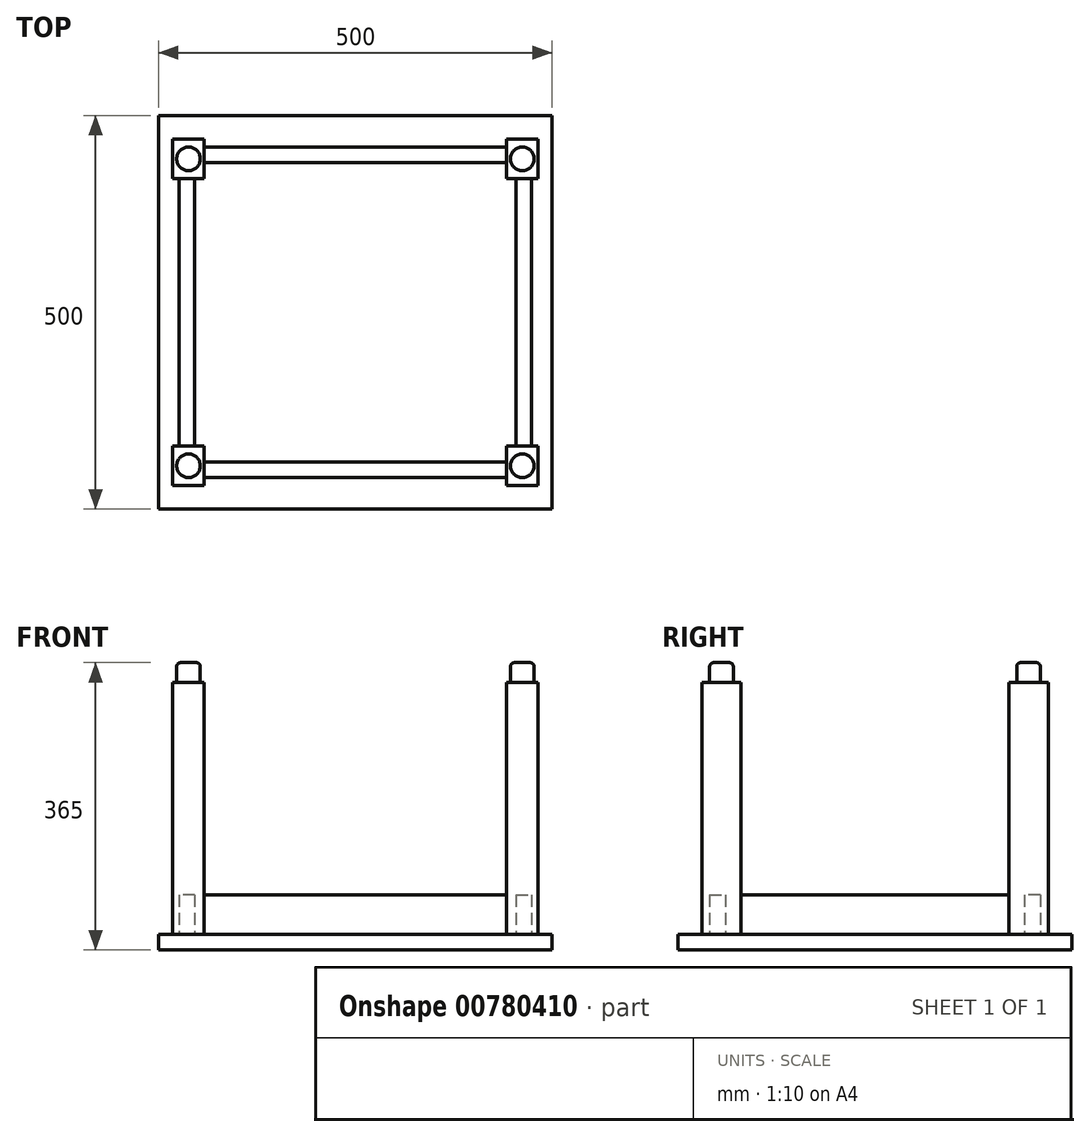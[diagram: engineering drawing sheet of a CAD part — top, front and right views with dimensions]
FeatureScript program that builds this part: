
annotation { "Feature Type Name" : "Feature", "Feature Type Description" : "" }
export const myFeature = defineFeature(function(context is Context, id is Id, definition is map)
    precondition{}
    {
        {
            var Q0;
            Q0=qCreatedBy(makeId("Top.planeOp"),FACE);
            var sketch = newSketch(context, id + "F0", { "sketchPlane" : qUnion([Q0])});
            skLineSegment(sketch, "E0.bottom", {"start": v(250, 250) * mm, "end": v(-250, 250) * mm});
            skLineSegment(sketch, "E0.top", {"start": v(250, -250) * mm, "end": v(-250, -250) * mm});
            skLineSegment(sketch, "E0.left", {"start": v(250, 250) * mm, "end": v(250, -250) * mm});
            skLineSegment(sketch, "E0.right", {"start": v(-250, 250) * mm, "end": v(-250, -250) * mm});
            skPoint(sketch, "E0.middle", {"position": v(0, 0) * mm});
            skSolve(sketch);
        }
        {
            var Q0;
            Q0 = qSketchRegion(id + "F0", true);
            extrude(context, id + "F1", {"entities" : qUnion([Q0]), "depth" : 20 * mm, "offsetDistance" : 25 * mm});
        }
        {
            var Q0;
            Q0=makeQuery(id+"F1.opExtrude","CAP_FACE",FACE,{"disambiguationData":[OSD([sQuery(id+"F0.wireOp",EDGE,"E0.bottom"),sQuery(id+"F0.wireOp",EDGE,"E0.top"),sQuery(id+"F0.wireOp",EDGE,"E0.left"),sQuery(id+"F0.wireOp",EDGE,"E0.right")])],"isStart":false});
            var sketch = newSketch(context, id + "F2", { "sketchPlane" : qUnion([Q0])});
            skLineSegment(sketch, "E1.bottom", {"start": v(212, 195) * mm, "end": v(-212, 195) * mm, "construction": true});
            skLineSegment(sketch, "E1.top", {"start": v(212, -195) * mm, "end": v(-212, -195) * mm, "construction": true});
            skLineSegment(sketch, "E1.left", {"start": v(212, 195) * mm, "end": v(212, -195) * mm, "construction": true});
            skLineSegment(sketch, "E1.right", {"start": v(-212, 195) * mm, "end": v(-212, -195) * mm, "construction": true});
            skPoint(sketch, "E1.middle", {"position": v(0, 0) * mm});
            skLineSegment(sketch, "E2.bottom", {"start": v(-192, 220) * mm, "end": v(-232, 220) * mm});
            skLineSegment(sketch, "E2.top", {"start": v(-192, 170) * mm, "end": v(-232, 170) * mm});
            skLineSegment(sketch, "E2.left", {"start": v(-192, 220) * mm, "end": v(-192, 170) * mm});
            skLineSegment(sketch, "E2.right", {"start": v(-232, 220) * mm, "end": v(-232, 170) * mm});
            skPoint(sketch, "E2.middle", {"position": v(-212, 195) * mm});
            skLineSegment(sketch, "E3", {"start": v(-212, 0) * mm, "end": v(212, 0) * mm, "construction": true});
            skLineSegment(sketch, "E4", {"start": v(0, 195) * mm, "end": v(0, -195) * mm, "construction": true});
            skLineSegment(sketch, "E5.MirrorCS", {"start": v(192, 220) * mm, "end": v(232, 220) * mm});
            skLineSegment(sketch, "E6.MirrorCS", {"start": v(192, 170) * mm, "end": v(232, 170) * mm});
            skLineSegment(sketch, "E7.MirrorCS", {"start": v(232, 220) * mm, "end": v(232, 170) * mm});
            skLineSegment(sketch, "E8.MirrorCS", {"start": v(192, 220) * mm, "end": v(192, 170) * mm});
            skPoint(sketch, "E9.MirrorP", {"position": v(212, 195) * mm});
            skLineSegment(sketch, "E10.MirrorCS", {"start": v(-212, 195) * mm, "end": v(212, 195) * mm, "construction": true});
            skLineSegment(sketch, "E11.MirrorCS", {"start": v(-192, -220) * mm, "end": v(-192, -170) * mm});
            skLineSegment(sketch, "E12.MirrorCS", {"start": v(192, -220) * mm, "end": v(192, -170) * mm});
            skPoint(sketch, "E13.MirrorP", {"position": v(-212, -195) * mm});
            skPoint(sketch, "E14.MirrorP", {"position": v(212, -195) * mm});
            skLineSegment(sketch, "E15.MirrorCS", {"start": v(232, -220) * mm, "end": v(232, -170) * mm});
            skLineSegment(sketch, "E16.MirrorCS", {"start": v(-232, -220) * mm, "end": v(-232, -170) * mm});
            skLineSegment(sketch, "E17.MirrorCS", {"start": v(-212, -195) * mm, "end": v(212, -195) * mm, "construction": true});
            skLineSegment(sketch, "E18.MirrorCS", {"start": v(192, -170) * mm, "end": v(232, -170) * mm});
            skLineSegment(sketch, "E19.MirrorCS", {"start": v(-192, -220) * mm, "end": v(-232, -220) * mm});
            skLineSegment(sketch, "E20.MirrorCS", {"start": v(-192, -170) * mm, "end": v(-232, -170) * mm});
            skLineSegment(sketch, "E21.MirrorCS", {"start": v(192, -220) * mm, "end": v(232, -220) * mm});
            skSolve(sketch);
        }
        {
            var Q0;
            Q0=makeQuery(id+"F2.imprint","IMPRINT",FACE,{"disambiguationData":[TD([[makeQuery(id+"F2.imprint","IMPRINT",EDGE,{"derivedFrom":sQuery(id+"F2.wireOp",EDGE,"E7.MirrorCS")}),-1.0]])]});
            var Q1;
            Q1=makeQuery(id+"F2.imprint","IMPRINT",FACE,{"disambiguationData":[TD([[makeQuery(id+"F2.imprint","IMPRINT",EDGE,{"derivedFrom":sQuery(id+"F2.wireOp",EDGE,"E11.MirrorCS")}),1.0]])]});
            var Q2;
            Q2=makeQuery(id+"F2.imprint","IMPRINT",FACE,{"disambiguationData":[TD([[makeQuery(id+"F2.imprint","IMPRINT",EDGE,{"derivedFrom":sQuery(id+"F2.wireOp",EDGE,"E15.MirrorCS")}),1.0]])]});
            var Q3;
            Q3=makeQuery(id+"F2.imprint","IMPRINT",FACE,{"disambiguationData":[TD([[makeQuery(id+"F2.imprint","IMPRINT",EDGE,{"derivedFrom":sQuery(id+"F2.wireOp",EDGE,"E2.left")}),-1.0]])]});
            extrude(context, id + "F3", {"entities" : qUnion([Q0, Q1, Q2, Q3]), "operationType" : NewBodyOperationType.ADD, "depth" : 320 * mm, "offsetDistance" : 25 * mm});
        }
        {
            var Q0;
            Q0=makeQuery(id+"F1.opExtrude","CAP_FACE",FACE,{"disambiguationData":[OSD([sQuery(id+"F0.wireOp",EDGE,"E0.bottom"),sQuery(id+"F0.wireOp",EDGE,"E0.top"),sQuery(id+"F0.wireOp",EDGE,"E0.left"),sQuery(id+"F0.wireOp",EDGE,"E0.right")])],"isStart":false});
            var sketch = newSketch(context, id + "F4", { "sketchPlane" : qUnion([Q0])});
            skLineSegment(sketch, "E22", {"start": v(-192, -210) * mm, "end": v(192, -210) * mm});
            skLineSegment(sketch, "E23", {"start": v(0, 0) * mm, "end": v(-294.35, 0) * mm, "construction": true});
            skLineSegment(sketch, "E24.MirrorCS", {"start": v(-192, 210) * mm, "end": v(-192, 199.43) * mm});
            skLineSegment(sketch, "E25.MirrorCS", {"start": v(192, 195) * mm, "end": v(192, 210) * mm});
            skLineSegment(sketch, "E26.MirrorCS", {"start": v(-192, 210) * mm, "end": v(192, 210) * mm});
            skLineSegment(sketch, "E27", {"start": v(-192, -190) * mm, "end": v(192, -190) * mm});
            skLineSegment(sketch, "E28", {"start": v(-192, -210) * mm, "end": v(-192, -190) * mm});
            skLineSegment(sketch, "E29", {"start": v(192, -210) * mm, "end": v(192, -190) * mm});
            skLineSegment(sketch, "E30", {"start": v(192, 210) * mm, "end": v(192, 190) * mm});
            skLineSegment(sketch, "E31", {"start": v(192, 190) * mm, "end": v(-192, 190) * mm});
            skLineSegment(sketch, "E32", {"start": v(-192, 190) * mm, "end": v(-192, 210) * mm});
            skLineSegment(sketch, "E33", {"start": v(-224, -170) * mm, "end": v(-224, 170) * mm});
            skLineSegment(sketch, "E34", {"start": v(-224, 170) * mm, "end": v(-204, 170) * mm});
            skLineSegment(sketch, "E35", {"start": v(-204, 170) * mm, "end": v(-204, -170) * mm});
            skLineSegment(sketch, "E36", {"start": v(-204, -170) * mm, "end": v(-224, -170) * mm});
            skLineSegment(sketch, "E37", {"start": v(0, 0) * mm, "end": v(0, -79.78) * mm, "construction": true});
            skLineSegment(sketch, "E38.MirrorCS", {"start": v(204, -170) * mm, "end": v(224, -170) * mm});
            skLineSegment(sketch, "E39.MirrorCS", {"start": v(224, 170) * mm, "end": v(204, 170) * mm});
            skLineSegment(sketch, "E40.MirrorCS", {"start": v(224, -170) * mm, "end": v(224, 170) * mm});
            skLineSegment(sketch, "E41.MirrorCS", {"start": v(204, 170) * mm, "end": v(204, -170) * mm});
            skSolve(sketch);
        }
        {
            var Q0;
            Q0=makeQuery(id+"F4.imprint","IMPRINT",FACE,{"disambiguationData":[TD([[makeQuery(id+"F4.imprint","IMPRINT",EDGE,{"derivedFrom":sQuery(id+"F4.wireOp",EDGE,"E22")}),1.0]])]});
            var Q1;
            {var subQ2=sQuery(id+"F4.wireOp",EDGE,"E26.MirrorCS");Q1=makeQuery(id+"F4.imprint","IMPRINT",FACE,{"disambiguationData":[TD([[makeQuery(id+"F4.imprint","IMPRINT",EDGE,{"derivedFrom":subQ2}),-1.0]])]});}
            var Q2;
            Q2=makeQuery(id+"F4.imprint","IMPRINT",FACE,{"disambiguationData":[TD([[makeQuery(id+"F4.imprint","IMPRINT",EDGE,{"derivedFrom":sQuery(id+"F4.wireOp",EDGE,"E38.MirrorCS")}),1.0]])]});
            var Q3;
            Q3=makeQuery(id+"F4.imprint","IMPRINT",FACE,{"disambiguationData":[TD([[makeQuery(id+"F4.imprint","IMPRINT",EDGE,{"derivedFrom":sQuery(id+"F4.wireOp",EDGE,"E33")}),-1.0]])]});
            extrude(context, id + "F5", {"entities" : qUnion([Q0, Q1, Q2, Q3]), "operationType" : NewBodyOperationType.ADD, "depth" : 50 * mm, "offsetDistance" : 25 * mm});
        }
        {
            var Q0;
            Q0=makeQuery(id+"F3.opExtrude","CAP_FACE",FACE,{"disambiguationData":[OSD([sQuery(id+"F2.wireOp",EDGE,"E7.MirrorCS"),sQuery(id+"F2.wireOp",EDGE,"E8.MirrorCS"),sQuery(id+"F2.wireOp",EDGE,"E6.MirrorCS"),sQuery(id+"F2.wireOp",EDGE,"E5.MirrorCS")])],"isStart":false});
            var sketch = newSketch(context, id + "F6", { "sketchPlane" : qUnion([Q0])});
            skLineSegment(sketch, "E42.0.0", {"start": v(232, 220) * mm, "end": v(192, 220) * mm});
            skLineSegment(sketch, "E42.0.1", {"start": v(192, 220) * mm, "end": v(192, 170) * mm});
            skLineSegment(sketch, "E42.0.2", {"start": v(192, 170) * mm, "end": v(232, 170) * mm});
            skLineSegment(sketch, "E42.0.3", {"start": v(232, 170) * mm, "end": v(232, 220) * mm});
            skLineSegment(sketch, "E43.0.0", {"start": v(192, -170) * mm, "end": v(192, -220) * mm});
            skLineSegment(sketch, "E43.0.1", {"start": v(192, -220) * mm, "end": v(232, -220) * mm});
            skLineSegment(sketch, "E43.0.2", {"start": v(232, -220) * mm, "end": v(232, -170) * mm});
            skLineSegment(sketch, "E43.0.3", {"start": v(232, -170) * mm, "end": v(192, -170) * mm});
            skLineSegment(sketch, "E44.0.0", {"start": v(-232, -170) * mm, "end": v(-232, -220) * mm});
            skLineSegment(sketch, "E44.0.1", {"start": v(-232, -220) * mm, "end": v(-192, -220) * mm});
            skLineSegment(sketch, "E44.0.2", {"start": v(-192, -220) * mm, "end": v(-192, -170) * mm});
            skLineSegment(sketch, "E44.0.3", {"start": v(-192, -170) * mm, "end": v(-232, -170) * mm});
            skLineSegment(sketch, "E45.0.0", {"start": v(-192, 220) * mm, "end": v(-232, 220) * mm});
            skLineSegment(sketch, "E45.0.1", {"start": v(-232, 220) * mm, "end": v(-232, 170) * mm});
            skLineSegment(sketch, "E45.0.2", {"start": v(-232, 170) * mm, "end": v(-192, 170) * mm});
            skLineSegment(sketch, "E45.0.3", {"start": v(-192, 170) * mm, "end": v(-192, 220) * mm});
            skSolve(sketch);
        }
        {
            var Q0;
            Q0=makeQuery(id+"F6.imprint","IMPRINT",FACE,{"disambiguationData":[TD([[makeQuery(id+"F6.imprint","IMPRINT",EDGE,{"derivedFrom":sQuery(id+"F6.wireOp",EDGE,"E43.0.0")}),1.0]])]});
            var sketch = newSketch(context, id + "F7", { "sketchPlane" : qUnion([Q0])});
            skLineSegment(sketch, "E46.0.0", {"start": v(232, -220) * mm, "end": v(232, -170) * mm, "construction": true});
            skLineSegment(sketch, "E46.0.1", {"start": v(232, -170) * mm, "end": v(192, -170) * mm, "construction": true});
            skLineSegment(sketch, "E46.0.2", {"start": v(192, -170) * mm, "end": v(192, -220) * mm, "construction": true});
            skLineSegment(sketch, "E46.0.3", {"start": v(192, -220) * mm, "end": v(232, -220) * mm, "construction": true});
            skLineSegment(sketch, "E47.0.0", {"start": v(-192, -220) * mm, "end": v(-192, -170) * mm, "construction": true});
            skLineSegment(sketch, "E47.0.1", {"start": v(-192, -170) * mm, "end": v(-232, -170) * mm, "construction": true});
            skLineSegment(sketch, "E47.0.2", {"start": v(-232, -170) * mm, "end": v(-232, -220) * mm, "construction": true});
            skLineSegment(sketch, "E47.0.3", {"start": v(-232, -220) * mm, "end": v(-192, -220) * mm, "construction": true});
            skLineSegment(sketch, "E48.0.0", {"start": v(-232, 170) * mm, "end": v(-192, 170) * mm, "construction": true});
            skLineSegment(sketch, "E48.0.1", {"start": v(-192, 170) * mm, "end": v(-192, 220) * mm, "construction": true});
            skLineSegment(sketch, "E48.0.2", {"start": v(-192, 220) * mm, "end": v(-232, 220) * mm, "construction": true});
            skLineSegment(sketch, "E48.0.3", {"start": v(-232, 220) * mm, "end": v(-232, 170) * mm, "construction": true});
            skLineSegment(sketch, "E49.0.0", {"start": v(232, 220) * mm, "end": v(192, 220) * mm, "construction": true});
            skLineSegment(sketch, "E49.0.1", {"start": v(192, 220) * mm, "end": v(192, 170) * mm, "construction": true});
            skLineSegment(sketch, "E49.0.2", {"start": v(192, 170) * mm, "end": v(232, 170) * mm, "construction": true});
            skLineSegment(sketch, "E49.0.3", {"start": v(232, 170) * mm, "end": v(232, 220) * mm, "construction": true});
            skCircle(sketch, "E50", {"center": v(212, 195) * mm, "radius": 15 * mm});
            skPoint(sketch, "E50.centerSnap0", {"position": v(192, 195) * mm});
            skPoint(sketch, "E50.centerSnap1", {"position": v(212, 170) * mm});
            skCircle(sketch, "E51.MirrorC", {"center": v(-212, 195) * mm, "radius": 15 * mm});
            skCircle(sketch, "E52.MirrorC", {"center": v(212, -195) * mm, "radius": 15 * mm});
            skCircle(sketch, "E53.MirrorC", {"center": v(-212, -195) * mm, "radius": 15 * mm});
            skSolve(sketch);
        }
        {
            var Q0;
            Q0 = qSketchRegion(id + "F7", true);
            extrude(context, id + "F8", {"entities" : qUnion([Q0]), "operationType" : NewBodyOperationType.ADD, "depth" : 25 * mm, "offsetDistance" : 25 * mm});
        }
        {
            var Q0;
            Q0=makeQuery(id+"F8.opExtrude","CAP_EDGE",EDGE,{"disambiguationData":[OSD([sQuery(id+"F7.wireOp",EDGE,"E50")])],"isStart":false});
            var Q1;
            Q1=makeQuery(id+"F8.opExtrude","CAP_EDGE",EDGE,{"disambiguationData":[OSD([sQuery(id+"F7.wireOp",EDGE,"E52.MirrorC")])],"isStart":false});
            var Q2;
            Q2=makeQuery(id+"F8.opExtrude","CAP_EDGE",EDGE,{"disambiguationData":[OSD([sQuery(id+"F7.wireOp",EDGE,"E53.MirrorC")])],"isStart":false});
            var Q3;
            Q3=makeQuery(id+"F8.opExtrude","CAP_EDGE",EDGE,{"disambiguationData":[OSD([sQuery(id+"F7.wireOp",EDGE,"E51.MirrorC")])],"isStart":false});
            fillet(context, id + "F9", {"entities" : qUnion([Q0, Q1, Q2, Q3]), "radius" : 5 * mm, "tangentPropagation" : true, "allowEdgeOverflow" : false});
        }
    });
